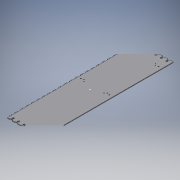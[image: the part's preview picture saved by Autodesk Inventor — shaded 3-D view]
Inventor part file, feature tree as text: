
AUTODESK INVENTOR PART (.ipt)
format: ipt  version: 2016 (Build 200138000, 138)  size: 520,192 bytes
history: native  units: in
note: dims shown in document units (in); Inventor stores cm internally (conversion verified against a paired STEP export)
features: extrude x10, sketch x10, pattern_linear x2, mirror x1
ambient origin geometry x8: Origin, YZ Plane, XZ Plane, XY Plane, X Axis, Y Axis, Z Axis, Center Point
bodies: Solid1 (feature_tree)
feature tree (23):
  extrude  "Extrusion1"  Depth=6.5in
  extrude  "Extrusion2"  Depth=0.5in
  extrude  "Extrusion3"  Depth=0.125in
  extrude  "Extrusion4"  Depth=0.14in
  extrude  "Extrusion5"  Depth=0.18in
  pattern_linear  "Rectangular Pattern1"  Spacing1=0.25in  [1 undecoded]
  sketch  "Sketch6"  dims[d12=0.25in d13=0.0in]
  mirror  "Mirror1"
  sketch  "Sketch7"  dims[d14=0.3125in]
  extrude  "Extrusion6"  Depth=0.14in
  extrude  "Extrusion7"  Depth=0.18in
  pattern_linear  "Rectangular Pattern2"  Spacing1=0.6in  [1 undecoded]
  extrude  "Extrusion9"  Depth=1.126in TaperAngle=0.0deg
  extrude  "Extrusion10"  Depth=1.0in
  extrude  "Extrusion12"  Depth=9.1811in
  sketch  "Sketch1"  dims[d0=24.125in d1=6.5in]
  sketch  "Sketch2"  dims[d2=0.125in d3=0.0in d4=0.5in]
  sketch  "Sketch3"  dims[d5=0.5in d6=0.125in]
  sketch  "Sketch4"  dims[d7=0.25in d8=0.0in d9=0.14in]
  sketch  "Sketch5"  dims[d10=0.2362in d11=0.18in]
  sketch  "Sketch12"  dims[d15=0.1094in]
  sketch  "Sketch13"  dims[d16=0.0in]
  sketch  "Sketch16"  dims[d17=0.0937in d18=0.25in d19=0.0in d20=0.14in d21=0.18in d22=0.6in d23=0.25in d24=0.0in d25=2.3622in d27=1.0in d28=9.1811in d29=4.0in d30=3.937in d31=4.8425in d36=0.2in d37=0.1575in d38=0.1575in d39=0.2in d40=0.1575in d41=0.1575in d42=0.2in d43=0.1575in d44=0.1575in d45=0.2in d46=0.1575in d47=0.1575in d55=0.125in d56=0.5in d57=0.0in d58=0.1575in d59=0.0in d60=0.125in d61=0.14in d62=0.181in d63=0.1575in d64=0.0in d65=9.0551in d67=1.0in d73=0.8287in d74=0.4213in d75=2.0in d76=2.2638in d77=0.1457in d78=0.15in d79=0.1614in d80=0.1457in d81=0.15in d82=0.1614in d83=0.1457in d84=0.15in d85=0.1614in d86=0.1457in d87=0.15in d88=0.1457in d89=0.15in d90=0.1614in d91=0.1457in d92=0.15in d93=0.1614in d94=0.1457in d95=0.15in d96=0.1614in d97=0.1457in d98=0.15in d99=0.1614in d107=0.3937in d108=0.0in d109=0.1614in d110=0.0in d111=0.0in d112=0.125in d114=0.3937in d115=0.0in d118=0.7874in d119=9.4488in d120=1.7717in d121=0.5512in d122=0.5512in d123=0.1969in d124=0.1969in d125=0.1969in d126=0.1969in d127=0.1969in d128=0.1969in d129=2.0866in d130=0.1969in d131=0.1969in d132=0.1969in d133=0.5512in d134=0.1969in d135=0.1969in d136=0.1969in d137=0.3937in d138=0.0in d139=1.126in]
note: 2 required parameter values undecoded (feature->parameter linkage not recoverable at this tier; creation-order binding heuristic only, values carry confidence <= 0.55)
